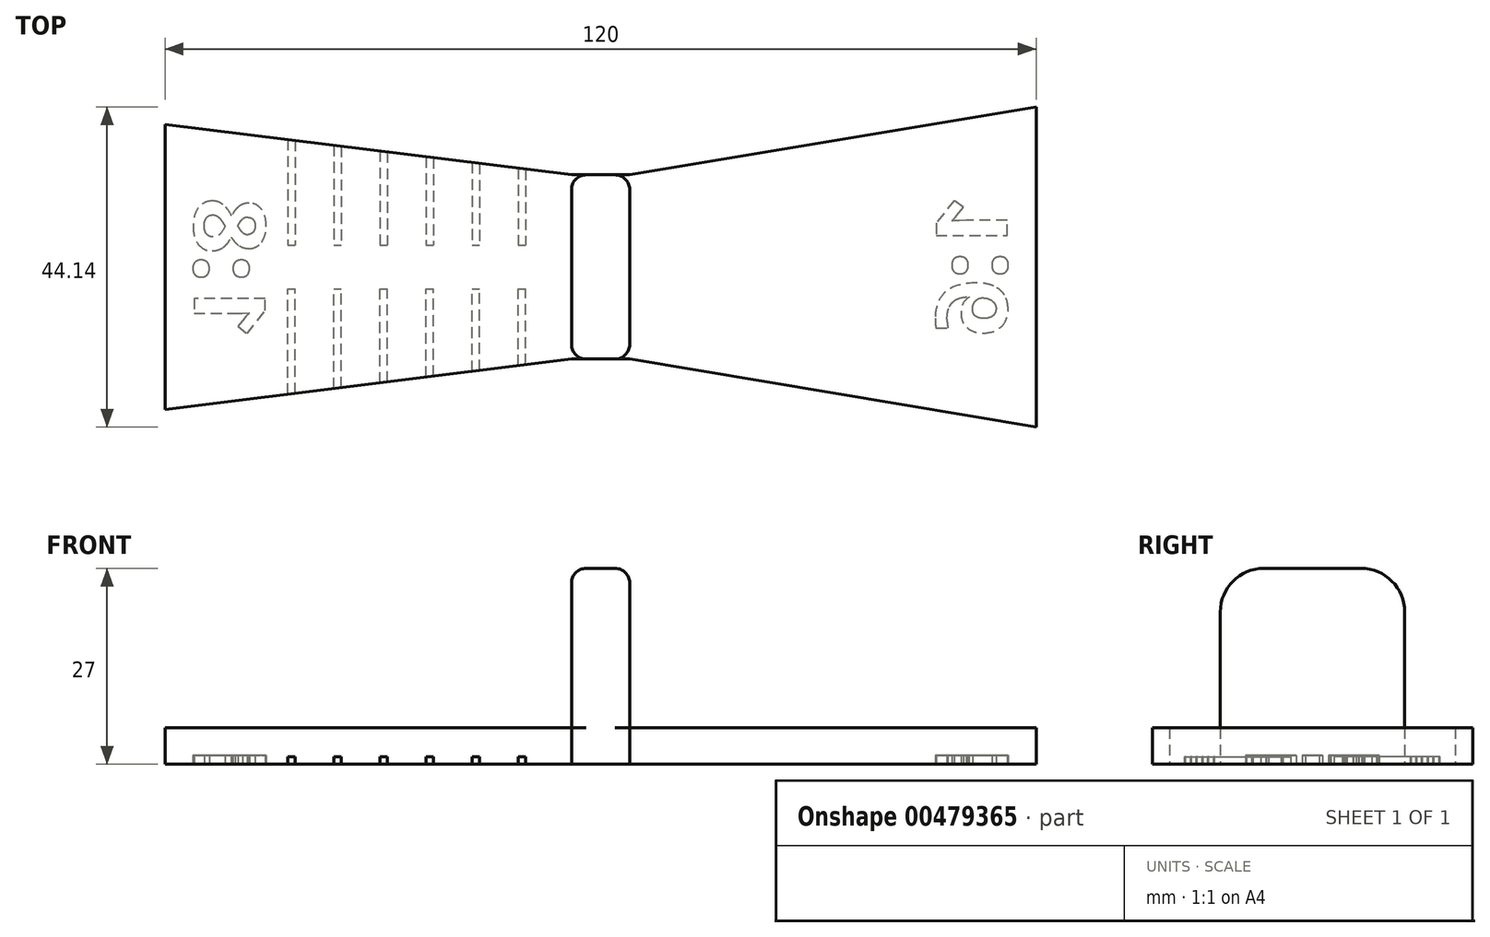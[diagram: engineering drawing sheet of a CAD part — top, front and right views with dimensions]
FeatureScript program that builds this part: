
annotation { "Feature Type Name" : "Feature", "Feature Type Description" : "" }
export const myFeature = defineFeature(function(context is Context, id is Id, definition is map)
    precondition{}
    {
        {
            var Q0;
            Q0=qCreatedBy(makeId("Top.planeOp"),FACE);
            var sketch = newSketch(context, id + "F0", { "sketchPlane" : qUnion([Q0])});
            skLineSegment(sketch, "E0", {"start": v(-4, 12.7) * mm, "end": v(-60, 19.68) * mm});
            skLineSegment(sketch, "E1", {"start": v(-60, 19.68) * mm, "end": v(-60, -19.68) * mm});
            skLineSegment(sketch, "E2", {"start": v(-60, -19.68) * mm, "end": v(-4, -12.7) * mm});
            skLineSegment(sketch, "E3", {"start": v(-4, -12.7) * mm, "end": v(4, -12.7) * mm});
            skLineSegment(sketch, "E4", {"start": v(4, -12.7) * mm, "end": v(60, -22.07) * mm});
            skLineSegment(sketch, "E5", {"start": v(60, -22.07) * mm, "end": v(60, 22.07) * mm});
            skLineSegment(sketch, "E6", {"start": v(60, 22.07) * mm, "end": v(4, 12.7) * mm});
            skLineSegment(sketch, "E7", {"start": v(4, 12.7) * mm, "end": v(-4, 12.7) * mm});
            skSolve(sketch);
        }
        {
            var Q0;
            Q0=makeQuery(id+"F0.imprint","IMPRINT",FACE,{"disambiguationData":[TD([[makeQuery(id+"F0.imprint","IMPRINT",EDGE,{"derivedFrom":sQuery(id+"F0.wireOp",EDGE,"E0")}),1.0]])]});
            extrude(context, id + "F1", {"entities" : qUnion([Q0]), "depth" : 5 * mm});
        }
        {
            var Q0;
            Q0=makeQuery(id+"F1.opExtrude","CAP_FACE",FACE,{"disambiguationData":[OSD([sQuery(id+"F0.wireOp",EDGE,"E0"),sQuery(id+"F0.wireOp",EDGE,"E1"),sQuery(id+"F0.wireOp",EDGE,"E2"),sQuery(id+"F0.wireOp",EDGE,"E3"),sQuery(id+"F0.wireOp",EDGE,"E4"),sQuery(id+"F0.wireOp",EDGE,"E5"),sQuery(id+"F0.wireOp",EDGE,"E6"),sQuery(id+"F0.wireOp",EDGE,"E7")])],"isStart":false});
            var sketch = newSketch(context, id + "F2", { "sketchPlane" : qUnion([Q0])});
            skLineSegment(sketch, "E8", {"start": v(-4, 12.7) * mm, "end": v(-4, -12.7) * mm});
            skLineSegment(sketch, "E9", {"start": v(-4, -12.7) * mm, "end": v(4, -12.7) * mm});
            skLineSegment(sketch, "E10", {"start": v(4, -12.7) * mm, "end": v(4, 12.7) * mm});
            skLineSegment(sketch, "E11", {"start": v(4, 12.7) * mm, "end": v(-4, 12.7) * mm});
            skSolve(sketch);
        }
        {
            var Q0;
            Q0=qSketchRegion(id+"F2",true);
            extrude(context, id + "F3", {"entities" : qUnion([Q0]), "operationType" : NewBodyOperationType.ADD, "depth" : 22 * mm});
        }
        {
            var Q0;
            Q0=makeQuery(id+"F3.opExtrude","CAP_EDGE",EDGE,{"disambiguationData":[OSD([sQuery(id+"F2.wireOp",EDGE,"E9")])],"isStart":false});
            var Q1;
            Q1=makeQuery(id+"F3.opExtrude","CAP_EDGE",EDGE,{"disambiguationData":[OSD([sQuery(id+"F2.wireOp",EDGE,"E11")])],"isStart":false});
            fillet(context, id + "F4", {"entities" : qUnion([Q0, Q1]), "radius" : 6 * mm, "tangentPropagation" : true, "allowEdgeOverflow" : false});
        }
        {
            var Q0;
            Q0=makeQuery(id+"F3.opExtrude","CAP_EDGE",EDGE,{"disambiguationData":[OSD([sQuery(id+"F2.wireOp",EDGE,"E8")])],"isStart":false});
            var Q1;
            Q1=makeQuery(id+"F3.opExtrude","CAP_EDGE",EDGE,{"disambiguationData":[OSD([sQuery(id+"F2.wireOp",EDGE,"E10")])],"isStart":false});
            fillet(context, id + "F5", {"entities" : qUnion([Q0, Q1]), "radius" : 2 * mm, "tangentPropagation" : true, "allowEdgeOverflow" : false});
        }
        {
            var Q0;
            Q0=makeQuery(id+"F1.opExtrude","CAP_FACE",FACE,{"disambiguationData":[OSD([sQuery(id+"F0.wireOp",EDGE,"E0"),sQuery(id+"F0.wireOp",EDGE,"E1"),sQuery(id+"F0.wireOp",EDGE,"E2"),sQuery(id+"F0.wireOp",EDGE,"E3"),sQuery(id+"F0.wireOp",EDGE,"E4"),sQuery(id+"F0.wireOp",EDGE,"E5"),sQuery(id+"F0.wireOp",EDGE,"E6"),sQuery(id+"F0.wireOp",EDGE,"E7")])],"isStart":true});
            var sketch = newSketch(context, id + "F6", { "sketchPlane" : qUnion([Q0])});
            skText(sketch, "E12", { "text": "1:8", "fontName": "OpenSans-Bold.ttf"});
            skText(sketch, "E13", { "text": "1:6", "fontName": "OpenSans-Bold.ttf"});
            const initialGuessF6  = {"E12": [-0.056, 0.01, 0, -1, 0.00988], "E13": [0.056, -0.01, 0, 1, 0.00986]};
            skSetInitialGuess(sketch, initialGuessF6);
            skSolve(sketch);
        }
        {
            var Q0;
            Q0=qSketchRegion(id+"F6",true);
            extrude(context, id + "F7", {"entities" : qUnion([Q0]), "operationType" : NewBodyOperationType.REMOVE, "oppositeDirection" : true, "depth" : 1.2 * mm});
        }
        {
            var Q0;
            {var subQ0=sQuery(id+"F0.wireOp",EDGE,"E7");var subQ1=sQuery(id+"F0.wireOp",EDGE,"E0");var subQ2=sQuery(id+"F0.wireOp",EDGE,"E6");var subQ3=sQuery(id+"F0.wireOp",EDGE,"E5");var subQ4=sQuery(id+"F0.wireOp",EDGE,"E4");var subQ5=sQuery(id+"F0.wireOp",EDGE,"E1");var subQ6=sQuery(id+"F0.wireOp",EDGE,"E2");var subQ7=sQuery(id+"F0.wireOp",EDGE,"E3");Q0=makeQuery(id+"F7.boolean.opBoolean","SPLIT",FACE,{"disambiguationData":[TD([makeQuery(id+"F1.opExtrude","SWEPT_FACE",FACE,{"disambiguationData":[OSD([subQ1])]})])],"derivedFrom":makeQuery(id+"F1.opExtrude","CAP_FACE",FACE,{"disambiguationData":[OSD([subQ1,subQ5,subQ6,subQ7,subQ4,subQ3,subQ2,subQ0])],"isStart":true})});}
            var sketch = newSketch(context, id + "F8", { "sketchPlane" : qUnion([Q0])});
            skLineSegment(sketch, "E14.bottom", {"start": v(-11.35, 23) * mm, "end": v(-10.35, 23) * mm});
            skLineSegment(sketch, "E14.top", {"start": v(-11.35, 3) * mm, "end": v(-10.35, 3) * mm});
            skLineSegment(sketch, "E14.left", {"start": v(-11.35, 23) * mm, "end": v(-11.35, 3) * mm});
            skLineSegment(sketch, "E14.right", {"start": v(-10.35, 23) * mm, "end": v(-10.35, 3) * mm});
            skLineSegment(sketch, "E15.1.0.0", {"start": v(-16.7, 23) * mm, "end": v(-16.7, 3) * mm});
            skLineSegment(sketch, "E15.1.0.1", {"start": v(-17.7, 23) * mm, "end": v(-16.7, 23) * mm});
            skLineSegment(sketch, "E15.1.0.2", {"start": v(-17.7, 23) * mm, "end": v(-17.7, 3) * mm});
            skLineSegment(sketch, "E15.1.0.3", {"start": v(-17.7, 3) * mm, "end": v(-16.7, 3) * mm});
            skLineSegment(sketch, "E15.2.0.0", {"start": v(-23.05, 23) * mm, "end": v(-23.05, 3) * mm});
            skLineSegment(sketch, "E15.2.0.1", {"start": v(-24.05, 23) * mm, "end": v(-23.05, 23) * mm});
            skLineSegment(sketch, "E15.2.0.2", {"start": v(-24.05, 23) * mm, "end": v(-24.05, 3) * mm});
            skLineSegment(sketch, "E15.2.0.3", {"start": v(-24.05, 3) * mm, "end": v(-23.05, 3) * mm});
            skLineSegment(sketch, "E15.3.0.0", {"start": v(-29.4, 23) * mm, "end": v(-29.4, 3) * mm});
            skLineSegment(sketch, "E15.3.0.1", {"start": v(-30.4, 23) * mm, "end": v(-29.4, 23) * mm});
            skLineSegment(sketch, "E15.3.0.2", {"start": v(-30.4, 23) * mm, "end": v(-30.4, 3) * mm});
            skLineSegment(sketch, "E15.3.0.3", {"start": v(-30.4, 3) * mm, "end": v(-29.4, 3) * mm});
            skLineSegment(sketch, "E15.4.0.0", {"start": v(-35.75, 23) * mm, "end": v(-35.75, 3) * mm});
            skLineSegment(sketch, "E15.4.0.1", {"start": v(-36.75, 23) * mm, "end": v(-35.75, 23) * mm});
            skLineSegment(sketch, "E15.4.0.2", {"start": v(-36.75, 23) * mm, "end": v(-36.75, 3) * mm});
            skLineSegment(sketch, "E15.4.0.3", {"start": v(-36.75, 3) * mm, "end": v(-35.75, 3) * mm});
            skLineSegment(sketch, "E15.direction1", {"start": v(-10.35, 3) * mm, "end": v(-16.7, 3) * mm, "construction": true});
            skLineSegment(sketch, "E16.0.5.0", {"start": v(-42.1, 23) * mm, "end": v(-42.1, 3) * mm});
            skLineSegment(sketch, "E16.3.5.0", {"start": v(-43.1, 23) * mm, "end": v(-42.1, 23) * mm});
            skLineSegment(sketch, "E16.6.5.0", {"start": v(-43.1, 23) * mm, "end": v(-43.1, 3) * mm});
            skLineSegment(sketch, "E16.9.5.0", {"start": v(-43.1, 3) * mm, "end": v(-42.1, 3) * mm});
            skLineSegment(sketch, "E17", {"start": v(-16.1, 0) * mm, "end": v(-40.75, 0) * mm, "construction": true});
            skLineSegment(sketch, "E18.MirrorCS", {"start": v(-30.4, -23) * mm, "end": v(-29.4, -23) * mm});
            skLineSegment(sketch, "E19.MirrorCS", {"start": v(-24.05, -23) * mm, "end": v(-23.05, -23) * mm});
            skLineSegment(sketch, "E20.MirrorCS", {"start": v(-30.4, -3) * mm, "end": v(-29.4, -3) * mm});
            skLineSegment(sketch, "E21.MirrorCS", {"start": v(-24.05, -3) * mm, "end": v(-23.05, -3) * mm});
            skLineSegment(sketch, "E22.MirrorCS", {"start": v(-43.1, -23) * mm, "end": v(-42.1, -23) * mm});
            skLineSegment(sketch, "E23.MirrorCS", {"start": v(-43.1, -3) * mm, "end": v(-42.1, -3) * mm});
            skLineSegment(sketch, "E24.MirrorCS", {"start": v(-36.75, -3) * mm, "end": v(-35.75, -3) * mm});
            skLineSegment(sketch, "E25.MirrorCS", {"start": v(-36.75, -23) * mm, "end": v(-35.75, -23) * mm});
            skLineSegment(sketch, "E26.MirrorCS", {"start": v(-36.75, -23) * mm, "end": v(-36.75, -3) * mm});
            skLineSegment(sketch, "E27.MirrorCS", {"start": v(-43.1, -23) * mm, "end": v(-43.1, -3) * mm});
            skLineSegment(sketch, "E28.MirrorCS", {"start": v(-30.4, -23) * mm, "end": v(-30.4, -3) * mm});
            skLineSegment(sketch, "E29.MirrorCS", {"start": v(-23.05, -23) * mm, "end": v(-23.05, -3) * mm});
            skLineSegment(sketch, "E30.MirrorCS", {"start": v(-42.1, -23) * mm, "end": v(-42.1, -3) * mm});
            skLineSegment(sketch, "E31.MirrorCS", {"start": v(-29.4, -23) * mm, "end": v(-29.4, -3) * mm});
            skLineSegment(sketch, "E32.MirrorCS", {"start": v(-24.05, -23) * mm, "end": v(-24.05, -3) * mm});
            skLineSegment(sketch, "E33.MirrorCS", {"start": v(-35.75, -23) * mm, "end": v(-35.75, -3) * mm});
            skLineSegment(sketch, "E34.MirrorCS", {"start": v(-17.7, -23) * mm, "end": v(-16.7, -23) * mm});
            skLineSegment(sketch, "E35.MirrorCS", {"start": v(-17.7, -23) * mm, "end": v(-17.7, -3) * mm});
            skLineSegment(sketch, "E36.MirrorCS", {"start": v(-16.7, -23) * mm, "end": v(-16.7, -3) * mm});
            skLineSegment(sketch, "E37.MirrorCS", {"start": v(-17.7, -3) * mm, "end": v(-16.7, -3) * mm});
            skLineSegment(sketch, "E38.MirrorCS", {"start": v(-11.35, -3) * mm, "end": v(-10.35, -3) * mm});
            skLineSegment(sketch, "E39.MirrorCS", {"start": v(-11.35, -23) * mm, "end": v(-11.35, -3) * mm});
            skLineSegment(sketch, "E40.MirrorCS", {"start": v(-10.35, -23) * mm, "end": v(-10.35, -3) * mm});
            skLineSegment(sketch, "E41.MirrorCS", {"start": v(-11.35, -23) * mm, "end": v(-10.35, -23) * mm});
            skSolve(sketch);
        }
        {
            var Q0;
            Q0=qSketchRegion(id+"F8",true);
            extrude(context, id + "F9", {"entities" : qUnion([Q0]), "operationType" : NewBodyOperationType.REMOVE, "oppositeDirection" : true, "depth" : 1 * mm});
        }
    });
